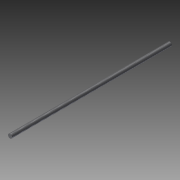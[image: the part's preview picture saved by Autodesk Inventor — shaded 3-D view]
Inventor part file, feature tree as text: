
AUTODESK INVENTOR PART (.ipt)
format: ipt  version: 2015 (Build 190159000, 159)  size: 68,096 bytes
history: native  units: mm
features: extrude x1, thread x1, sketch x1
ambient origin geometry x8: Origin, YZ Plane, XZ Plane, XY Plane, X Axis, Y Axis, Z Axis, Center Point
bodies: Solid1 (feature_tree)
feature tree (3):
  extrude  "Extrusion1"  Depth=310.0mm TaperAngle=0.0deg
  thread  "Thread1"  [1 undecoded]
  sketch  "Sketch1"  dims[d0=8.0mm d1=310.0mm d2=0.0mm d3=10.0mm d4=0.0mm]
note: 1 required parameter value undecoded (feature->parameter linkage not recoverable at this tier; creation-order binding heuristic only, values carry confidence <= 0.55)
